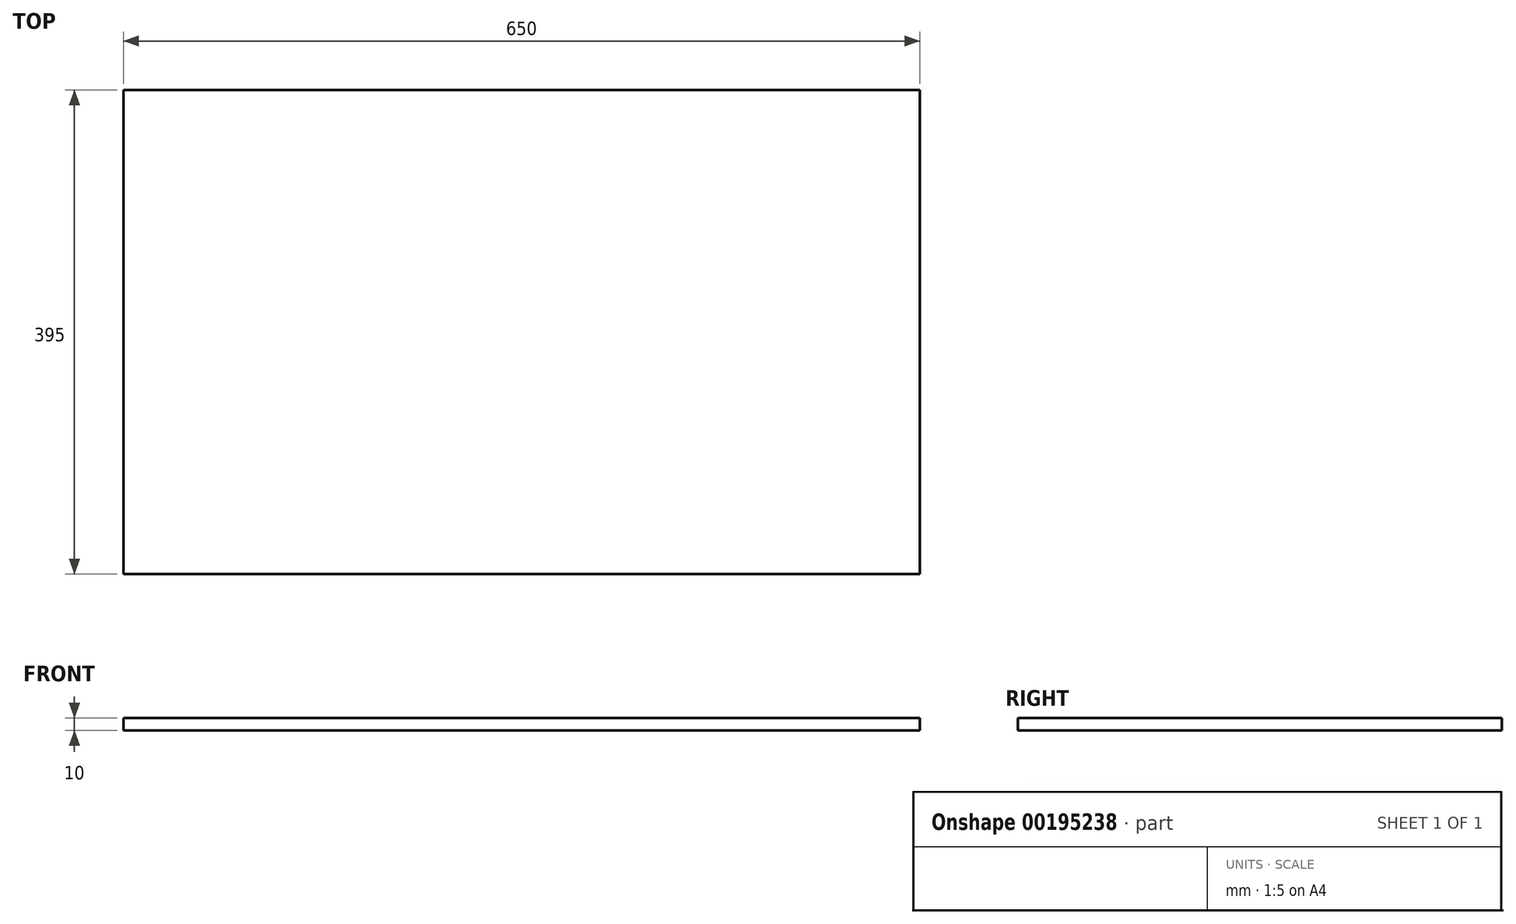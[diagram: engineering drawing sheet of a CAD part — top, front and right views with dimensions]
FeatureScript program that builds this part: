
annotation { "Feature Type Name" : "Feature", "Feature Type Description" : "" }
export const myFeature = defineFeature(function(context is Context, id is Id, definition is map)
    precondition{}
    {
        {
            var Q0;
            Q0=qCreatedBy(makeId("Top.planeOp"),FACE);
            var sketch = newSketch(context, id + "F1", { "sketchPlane" : qUnion([Q0])});
            skLineSegment(sketch, "E0.bottom", {"start": v(-325, 197.5) * mm, "end": v(325, 197.5) * mm});
            skLineSegment(sketch, "E0.top", {"start": v(-325, -197.5) * mm, "end": v(325, -197.5) * mm});
            skLineSegment(sketch, "E0.left", {"start": v(-325, 197.5) * mm, "end": v(-325, -197.5) * mm});
            skLineSegment(sketch, "E0.right", {"start": v(325, 197.5) * mm, "end": v(325, -197.5) * mm});
            skPoint(sketch, "E0.middle", {"position": v(0, 0) * mm});
            skSolve(sketch);
        }
        {
            var Q0;
            Q0=makeQuery(id+"F1.imprint","IMPRINT",FACE,{"disambiguationData":[TD([[makeQuery(id+"F1.imprint","IMPRINT",EDGE,{"derivedFrom":sQuery(id+"F1.wireOp",EDGE,"E0.bottom")}),-1.0]])]});
            extrude(context, id + "F0", {"entities" : qUnion([Q0]), "depth" : 10 * mm});
        }
    });
